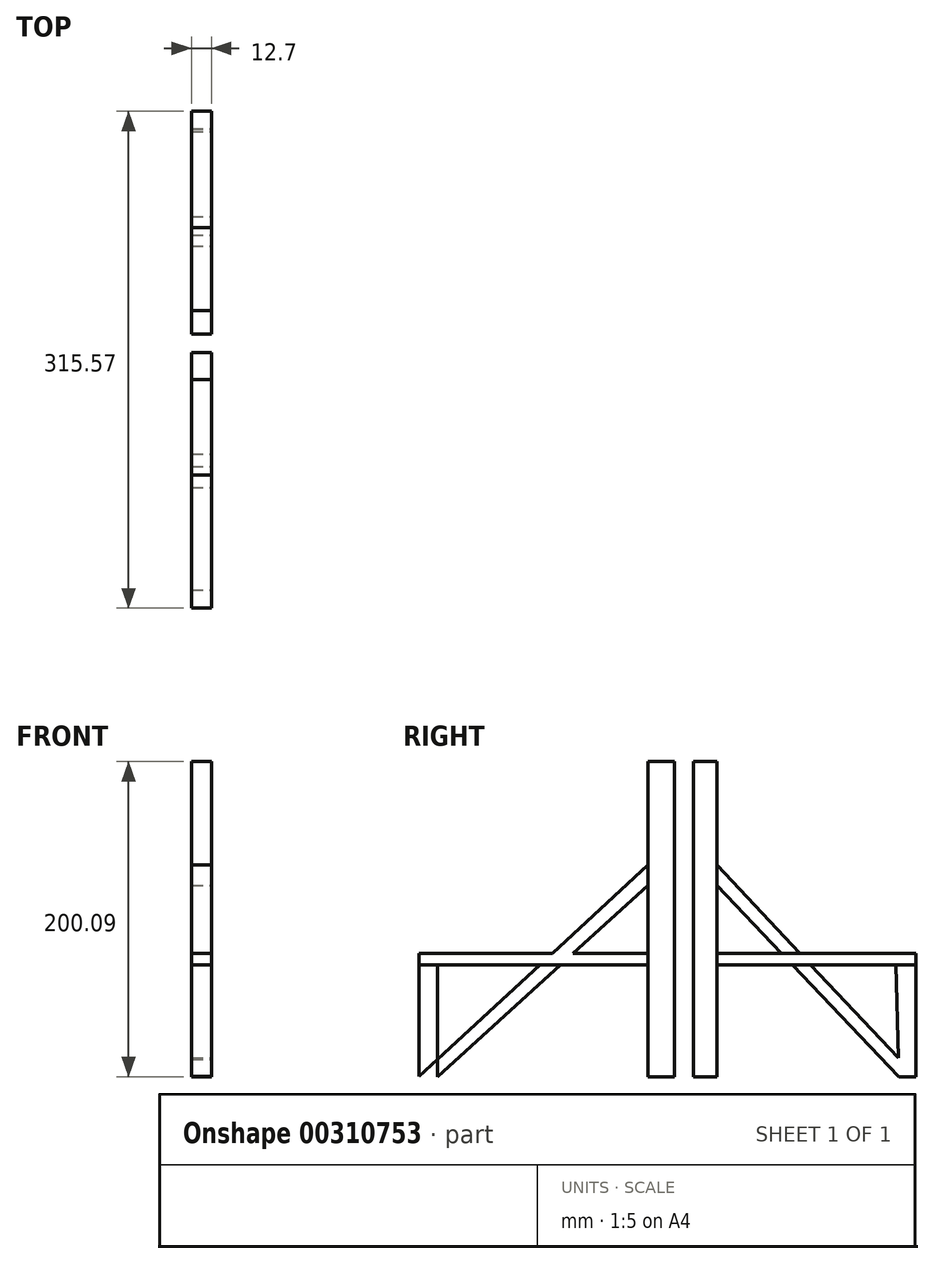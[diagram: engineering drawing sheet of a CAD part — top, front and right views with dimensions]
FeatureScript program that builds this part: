
annotation { "Feature Type Name" : "Feature", "Feature Type Description" : "" }
export const myFeature = defineFeature(function(context is Context, id is Id, definition is map)
    precondition{}
    {
        {
            var Q0;
            Q0=qCreatedBy(makeId("Right.planeOp"),FACE);
            var sketch = newSketch(context, id + "F0", { "sketchPlane" : qUnion([Q0])});
            skLineSegment(sketch, "E0.bottom", {"start": v(165.95, 5.46) * mm, "end": v(-138, 5.46) * mm});
            skLineSegment(sketch, "E0.top", {"start": v(165.95, -65.61) * mm, "end": v(-138, -65.61) * mm});
            skLineSegment(sketch, "E0.left", {"start": v(165.95, 5.46) * mm, "end": v(165.95, -65.61) * mm});
            skLineSegment(sketch, "E0.right", {"start": v(-138, 5.46) * mm, "end": v(-138, -65.61) * mm});
            skLineSegment(sketch, "E1", {"start": v(39.53, -65.61) * mm, "end": v(39.53, 134.48) * mm});
            skLineSegment(sketch, "E2", {"start": v(-4.28, -65.61) * mm, "end": v(-4.28, 134.48) * mm});
            skLineSegment(sketch, "E3", {"start": v(39.53, 134.48) * mm, "end": v(24.6, 134.48) * mm});
            skLineSegment(sketch, "E4", {"start": v(24.6, 134.48) * mm, "end": v(24.6, -65.61) * mm});
            skLineSegment(sketch, "E5", {"start": v(-4.28, 134.48) * mm, "end": v(12.65, 134.48) * mm});
            skLineSegment(sketch, "E6", {"start": v(12.65, 134.48) * mm, "end": v(12.65, -65.61) * mm});
            skLineSegment(sketch, "E7", {"start": v(39.53, 68.78) * mm, "end": v(165.95, -65.61) * mm});
            skLineSegment(sketch, "E8", {"start": v(39.53, 55.84) * mm, "end": v(155, -65.61) * mm});
            skLineSegment(sketch, "E9", {"start": v(-138, 5.46) * mm, "end": v(-149.61, 5.46) * mm});
            skLineSegment(sketch, "E10", {"start": v(-149.61, 5.46) * mm, "end": v(-149.61, -65.42) * mm});
            skLineSegment(sketch, "E11", {"start": v(-149.61, -65.42) * mm, "end": v(-138, -65.61) * mm});
            skLineSegment(sketch, "E12", {"start": v(-149.61, 5.46) * mm, "end": v(-149.61, 12.73) * mm});
            skLineSegment(sketch, "E13", {"start": v(-149.61, 12.73) * mm, "end": v(-4.28, 12.73) * mm});
            skLineSegment(sketch, "E14", {"start": v(39.53, 12.73) * mm, "end": v(165.96, 12.73) * mm});
            skLineSegment(sketch, "E15", {"start": v(165.96, 12.73) * mm, "end": v(165.95, 5.46) * mm});
            skLineSegment(sketch, "E16", {"start": v(-4.28, 55.87) * mm, "end": v(-138, -65.61) * mm});
            skLineSegment(sketch, "E17", {"start": v(-4.28, 68.78) * mm, "end": v(-149.61, -65.42) * mm});
            skLineSegment(sketch, "E18", {"start": v(153.11, 5.46) * mm, "end": v(155, -65.61) * mm});
            skLineSegment(sketch, "E19", {"start": v(165.95, -65.61) * mm, "end": v(165.95, -68.96) * mm});
            skLineSegment(sketch, "E20", {"start": v(165.95, -68.96) * mm, "end": v(-149.61, -68.96) * mm});
            skLineSegment(sketch, "E21", {"start": v(-149.61, -65.42) * mm, "end": v(-149.61, -68.96) * mm});
            skSolve(sketch);
        }
        {
            var Q0;
            {var subQ0=sQuery(id+"F0.wireOp",EDGE,"E4");var subQ1=sQuery(id+"F0.wireOp",EDGE,"E0.bottom");var subQ2=makeQuery(id+"F0.imprint","INTERSECT",VERTEX,{"derivedFrom":[subQ1,subQ0]});Q0=makeQuery(id+"F0.imprint","IMPRINT",FACE,{"disambiguationData":[TD([[makeQuery(id+"F0.imprint","IMPRINT",EDGE,{"disambiguationData":[TD([[subQ2,1.0]])],"derivedFrom":subQ1}),1.0]])]});}
            var Q1;
            {var subQ0=sQuery(id+"F0.wireOp",EDGE,"E6");var subQ1=sQuery(id+"F0.wireOp",EDGE,"E0.bottom");var subQ2=makeQuery(id+"F0.imprint","INTERSECT",VERTEX,{"derivedFrom":[subQ1,subQ0]});Q1=makeQuery(id+"F0.imprint","IMPRINT",FACE,{"disambiguationData":[TD([[makeQuery(id+"F0.imprint","IMPRINT",EDGE,{"disambiguationData":[TD([[subQ2,-1.0]])],"derivedFrom":subQ1}),1.0]])]});}
            var Q2;
            {var subQ0=sQuery(id+"F0.wireOp",EDGE,"E9");Q2=makeQuery(id+"F0.imprint","IMPRINT",FACE,{"disambiguationData":[TD([[makeQuery(id+"F0.imprint","IMPRINT",EDGE,{"derivedFrom":subQ0}),1.0]])]});}
            var Q3;
            {var subQ0=sQuery(id+"F0.wireOp",EDGE,"E0.left");Q3=makeQuery(id+"F0.imprint","IMPRINT",FACE,{"disambiguationData":[TD([[makeQuery(id+"F0.imprint","IMPRINT",EDGE,{"derivedFrom":subQ0}),-1.0]])]});}
            var Q4;
            {var subQ0=sQuery(id+"F0.wireOp",EDGE,"E7");var subQ3=sQuery(id+"F0.wireOp",EDGE,"E18");var subQ5=makeQuery(id+"F0.imprint","INTERSECT",VERTEX,{"derivedFrom":[subQ0,subQ3]});Q4=makeQuery(id+"F0.imprint","IMPRINT",FACE,{"disambiguationData":[TD([[makeQuery(id+"F0.imprint","IMPRINT",EDGE,{"disambiguationData":[TD([[subQ5,-1.0]])],"derivedFrom":subQ3}),1.0]])]});}
            var Q5;
            {var subQ0=sQuery(id+"F0.wireOp",EDGE,"E7");var subQ1=sQuery(id+"F0.wireOp",EDGE,"E0.bottom");var subQ2=makeQuery(id+"F0.imprint","INTERSECT",VERTEX,{"derivedFrom":[subQ1,subQ0]});Q5=makeQuery(id+"F0.imprint","IMPRINT",FACE,{"disambiguationData":[TD([[makeQuery(id+"F0.imprint","IMPRINT",EDGE,{"disambiguationData":[TD([[subQ2,-1.0]])],"derivedFrom":subQ1}),1.0]])]});}
            var Q6;
            {var subQ0=sQuery(id+"F0.wireOp",EDGE,"E16");var subQ1=sQuery(id+"F0.wireOp",EDGE,"E0.bottom");var subQ2=makeQuery(id+"F0.imprint","INTERSECT",VERTEX,{"derivedFrom":[subQ1,subQ0]});Q6=makeQuery(id+"F0.imprint","IMPRINT",FACE,{"disambiguationData":[TD([[makeQuery(id+"F0.imprint","IMPRINT",EDGE,{"disambiguationData":[TD([[subQ2,-1.0]])],"derivedFrom":subQ1}),1.0]])]});}
            var Q7;
            {var subQ8=sQuery(id+"F0.wireOp",EDGE,"E5");Q7=makeQuery(id+"F0.imprint","IMPRINT",FACE,{"disambiguationData":[TD([[makeQuery(id+"F0.imprint","IMPRINT",EDGE,{"derivedFrom":subQ8}),-1.0]])]});}
            var Q8;
            {var subQ8=sQuery(id+"F0.wireOp",EDGE,"E3");Q8=makeQuery(id+"F0.imprint","IMPRINT",FACE,{"disambiguationData":[TD([[makeQuery(id+"F0.imprint","IMPRINT",EDGE,{"derivedFrom":subQ8}),1.0]])]});}
            var Q9;
            Q9=sQuery(id+"F0.wireOp",EDGE,"E0.bottom");
            var Q10;
            Q10=sQuery(id+"F0.wireOp",EDGE,"E0.top");
            var Q11;
            Q11=sQuery(id+"F0.wireOp",EDGE,"E0.left");
            var Q12;
            Q12=sQuery(id+"F0.wireOp",EDGE,"E0.right");
            var Q13;
            Q13=sQuery(id+"F0.wireOp",EDGE,"E1");
            var Q14;
            Q14=sQuery(id+"F0.wireOp",EDGE,"E2");
            var Q15;
            Q15=sQuery(id+"F0.wireOp",EDGE,"E3");
            var Q16;
            Q16=sQuery(id+"F0.wireOp",EDGE,"E4");
            var Q17;
            Q17=sQuery(id+"F0.wireOp",EDGE,"E5");
            var Q18;
            Q18=sQuery(id+"F0.wireOp",EDGE,"E6");
            var Q19;
            Q19=sQuery(id+"F0.wireOp",EDGE,"E7");
            var Q20;
            Q20=sQuery(id+"F0.wireOp",EDGE,"E8");
            var Q21;
            Q21=sQuery(id+"F0.wireOp",EDGE,"E9");
            var Q22;
            Q22=sQuery(id+"F0.wireOp",EDGE,"E10");
            var Q23;
            Q23=sQuery(id+"F0.wireOp",EDGE,"E11");
            var Q24;
            Q24=sQuery(id+"F0.wireOp",EDGE,"E12");
            var Q25;
            Q25=sQuery(id+"F0.wireOp",EDGE,"E13");
            var Q26;
            Q26=sQuery(id+"F0.wireOp",EDGE,"E14");
            var Q27;
            Q27=sQuery(id+"F0.wireOp",EDGE,"E15");
            var Q28;
            Q28=sQuery(id+"F0.wireOp",EDGE,"E16");
            var Q29;
            Q29=sQuery(id+"F0.wireOp",EDGE,"E17");
            var Q30;
            Q30=sQuery(id+"F0.wireOp",EDGE,"E18");
            var Q31;
            Q31=sQuery(id+"F0.wireOp",EDGE,"E19");
            var Q32;
            Q32=sQuery(id+"F0.wireOp",EDGE,"E20");
            var Q33;
            Q33=sQuery(id+"F0.wireOp",EDGE,"E21");
            extrude(context, id + "F1", {"entities" : qUnion([Q0, Q1, Q2, Q3, Q4, Q5, Q6, Q7, Q8]), "surfaceEntities" : qUnion([Q9, Q10, Q11, Q12, Q13, Q14, Q15, Q16, Q17, Q18, Q19, Q20, Q21, Q22, Q23, Q24, Q25, Q26, Q27, Q28, Q29, Q30, Q31, Q32, Q33]), "oppositeDirection" : true, "depth" : 12.7 * mm});
        }
        {
            var Q0;
            {var subQ0=sQuery(id+"F0.wireOp",EDGE,"E16");var subQ1=sQuery(id+"F0.wireOp",EDGE,"E2");var subQ2=makeQuery(id+"F0.imprint","INTERSECT",VERTEX,{"derivedFrom":[subQ1,subQ0]});Q0=makeQuery(id+"F0.imprint","IMPRINT",FACE,{"disambiguationData":[TD([[makeQuery(id+"F0.imprint","IMPRINT",EDGE,{"disambiguationData":[TD([[subQ2,-1.0]])],"derivedFrom":subQ1}),1.0]])]});}
            var Q1;
            {var subQ6=sQuery(id+"F0.wireOp",EDGE,"E9");Q1=makeQuery(id+"F0.imprint","IMPRINT",FACE,{"disambiguationData":[TD([[makeQuery(id+"F0.imprint","IMPRINT",EDGE,{"derivedFrom":subQ6}),-1.0]])]});}
            var Q2;
            {var subQ0=sQuery(id+"F0.wireOp",EDGE,"E2");var subQ1=sQuery(id+"F0.wireOp",EDGE,"E0.bottom");var subQ2=makeQuery(id+"F0.imprint","INTERSECT",VERTEX,{"derivedFrom":[subQ1,subQ0]});Q2=makeQuery(id+"F0.imprint","IMPRINT",FACE,{"disambiguationData":[TD([[makeQuery(id+"F0.imprint","IMPRINT",EDGE,{"disambiguationData":[TD([[subQ2,-1.0]])],"derivedFrom":subQ1}),-1.0]])]});}
            var Q3;
            {var subQ0=sQuery(id+"F0.wireOp",EDGE,"E16");var subQ1=sQuery(id+"F0.wireOp",EDGE,"E0.bottom");var subQ2=makeQuery(id+"F0.imprint","INTERSECT",VERTEX,{"derivedFrom":[subQ1,subQ0]});Q3=makeQuery(id+"F0.imprint","IMPRINT",FACE,{"disambiguationData":[TD([[makeQuery(id+"F0.imprint","IMPRINT",EDGE,{"disambiguationData":[TD([[subQ2,-1.0]])],"derivedFrom":subQ1}),-1.0]])]});}
            var Q4;
            {var subQ0=sQuery(id+"F0.wireOp",EDGE,"E7");var subQ1=sQuery(id+"F0.wireOp",EDGE,"E1");var subQ2=makeQuery(id+"F0.imprint","INTERSECT",VERTEX,{"derivedFrom":[subQ1,subQ0]});Q4=makeQuery(id+"F0.imprint","IMPRINT",FACE,{"disambiguationData":[TD([[makeQuery(id+"F0.imprint","IMPRINT",EDGE,{"disambiguationData":[TD([[subQ2,1.0]])],"derivedFrom":subQ1}),-1.0]])]});}
            extrude(context, id + "F2", {"entities" : qUnion([Q0, Q1, Q2, Q3, Q4]), "oppositeDirection" : true, "depth" : 12.7 * mm});
        }
        {
            var Q0;
            {var subQ0=sQuery(id+"F0.wireOp",EDGE,"E8");var subQ1=sQuery(id+"F0.wireOp",EDGE,"E0.bottom");var subQ2=makeQuery(id+"F0.imprint","INTERSECT",VERTEX,{"derivedFrom":[subQ1,subQ0]});Q0=makeQuery(id+"F0.imprint","IMPRINT",FACE,{"disambiguationData":[TD([[makeQuery(id+"F0.imprint","IMPRINT",EDGE,{"disambiguationData":[TD([[subQ2,-1.0]])],"derivedFrom":subQ1}),-1.0]])]});}
            var Q1;
            {var subQ0=sQuery(id+"F0.wireOp",EDGE,"E15");Q1=makeQuery(id+"F0.imprint","IMPRINT",FACE,{"disambiguationData":[TD([[makeQuery(id+"F0.imprint","IMPRINT",EDGE,{"derivedFrom":subQ0}),-1.0]])]});}
            var Q2;
            {var subQ0=sQuery(id+"F0.wireOp",EDGE,"E7");var subQ1=sQuery(id+"F0.wireOp",EDGE,"E0.bottom");var subQ2=makeQuery(id+"F0.imprint","INTERSECT",VERTEX,{"derivedFrom":[subQ1,subQ0]});Q2=makeQuery(id+"F0.imprint","IMPRINT",FACE,{"disambiguationData":[TD([[makeQuery(id+"F0.imprint","IMPRINT",EDGE,{"disambiguationData":[TD([[subQ2,-1.0]])],"derivedFrom":subQ1}),-1.0]])]});}
            extrude(context, id + "F3", {"entities" : qUnion([Q0, Q1, Q2]), "oppositeDirection" : true, "depth" : 12.7 * mm});
        }
    });
